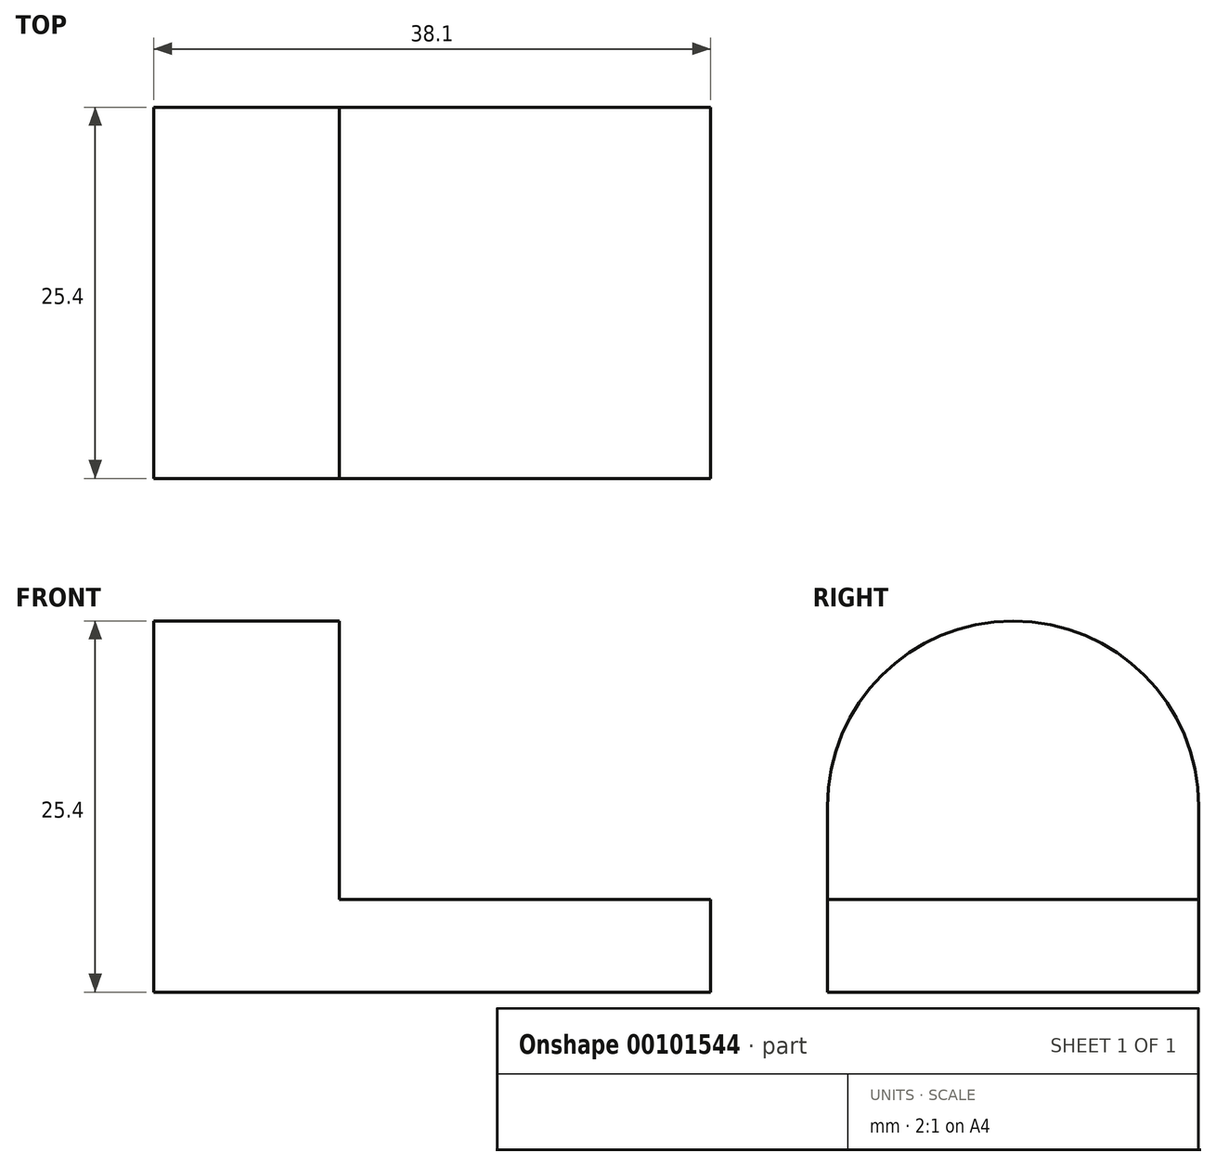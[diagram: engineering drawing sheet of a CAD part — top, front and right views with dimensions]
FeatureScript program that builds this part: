
annotation { "Feature Type Name" : "Feature", "Feature Type Description" : "" }
export const myFeature = defineFeature(function(context is Context, id is Id, definition is map)
    precondition{}
    {
        {
            var Q0;
            Q0=qCreatedBy(makeId("Top.planeOp"),FACE);
            var sketch = newSketch(context, id + "F0", { "sketchPlane" : qUnion([Q0])});
            skLineSegment(sketch, "E0", {"start": v(0, 0) * mm, "end": v(38.1, 0) * mm});
            skLineSegment(sketch, "E1", {"start": v(38.1, 0) * mm, "end": v(38.1, 25.4) * mm});
            skLineSegment(sketch, "E2", {"start": v(38.1, 25.4) * mm, "end": v(0, 25.4) * mm});
            skLineSegment(sketch, "E3", {"start": v(0, 25.4) * mm, "end": v(0, 0) * mm});
            skSolve(sketch);
        }
        {
            var Q0;
            Q0=makeQuery(id+"F0.imprint","IMPRINT",FACE,{"disambiguationData":[TD([[makeQuery(id+"F0.imprint","IMPRINT",EDGE,{"derivedFrom":sQuery(id+"F0.wireOp",EDGE,"E0")}),1.0]])]});
            extrude(context, id + "F1", {"entities" : qUnion([Q0]), "oppositeDirection" : true, "depth" : 6.35 * mm});
        }
        {
            var Q0;
            Q0=qCreatedBy(makeId("Right.planeOp"),FACE);
            var sketch = newSketch(context, id + "F2", { "sketchPlane" : qUnion([Q0])});
            skLineSegment(sketch, "E4", {"start": v(0, 0) * mm, "end": v(0, 6.35) * mm});
            skLineSegment(sketch, "E5", {"start": v(25.4, 6.35) * mm, "end": v(25.4, 0) * mm});
            skArc(sketch, "E6", {"start": v(0, 6.35) * mm, "mid": v(12.7, 19.05) * mm, "end": v(25.4, 6.35) * mm});
            skLineSegment(sketch, "E7", {"start": v(0, 0) * mm, "end": v(25.4, 0) * mm});
            skSolve(sketch);
        }
        {
            var Q0;
            Q0=makeQuery(id+"F2.imprint","IMPRINT",FACE,{"disambiguationData":[TD([[makeQuery(id+"F2.imprint","IMPRINT",EDGE,{"derivedFrom":sQuery(id+"F2.wireOp",EDGE,"E4")}),-1.0]])]});
            extrude(context, id + "F3", {"entities" : qUnion([Q0]), "operationType" : NewBodyOperationType.ADD, "depth" : 12.7 * mm});
        }
    });
